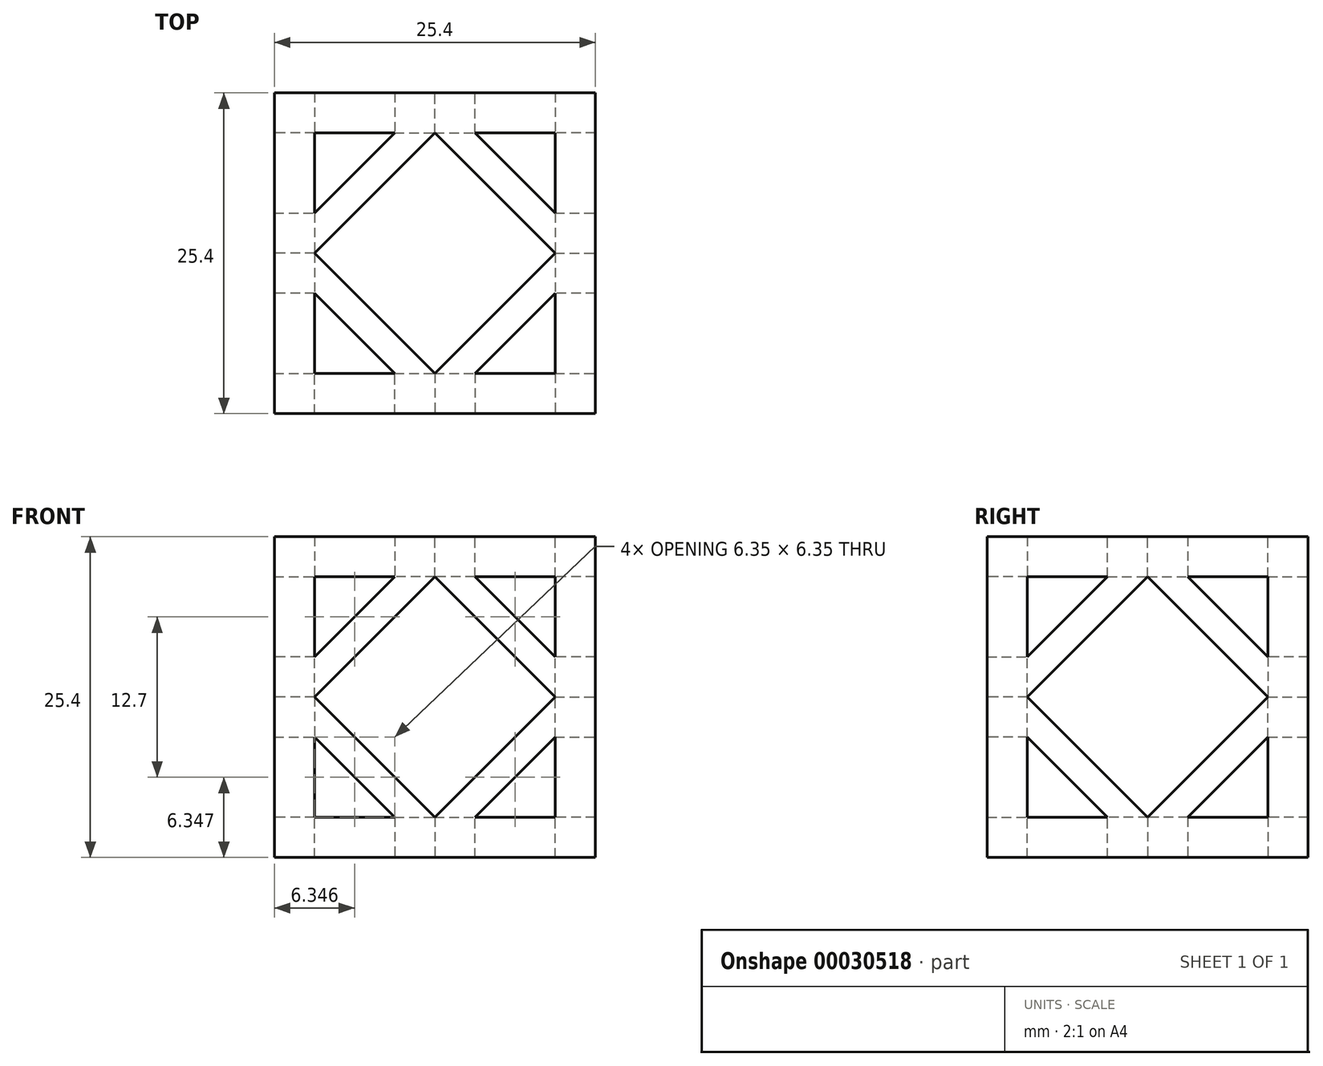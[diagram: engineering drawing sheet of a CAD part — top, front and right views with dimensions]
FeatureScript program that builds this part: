
annotation { "Feature Type Name" : "Feature", "Feature Type Description" : "" }
export const myFeature = defineFeature(function(context is Context, id is Id, definition is map)
    precondition{}
    {
        {
            var Q0;
            Q0=qCreatedBy(makeId("Front.planeOp"),FACE);
            var sketch = newSketch(context, id + "F0", { "sketchPlane" : qUnion([Q0])});
            skLineSegment(sketch, "E0.bottom", {"start": v(-17.45, 16.02) * mm, "end": v(7.95, 16.02) * mm});
            skLineSegment(sketch, "E0.top", {"start": v(-17.45, -9.38) * mm, "end": v(7.95, -9.38) * mm});
            skLineSegment(sketch, "E0.left", {"start": v(-17.45, 16.02) * mm, "end": v(-17.45, -9.38) * mm});
            skLineSegment(sketch, "E0.right", {"start": v(7.95, 16.02) * mm, "end": v(7.95, -9.38) * mm});
            skSolve(sketch);
        }
        {
            var Q0;
            Q0 = qSketchRegion(id + "F0", true);
            extrude(context, id + "F1", {"entities" : qUnion([Q0]), "depth" : 25.4 * mm});
        }
        {
            var Q0;
            Q0=makeQuery(id+"F1.opExtrude","CAP_FACE",FACE,{"disambiguationData":[OSD([sQuery(id+"F0.wireOp",EDGE,"E0.bottom"),sQuery(id+"F0.wireOp",EDGE,"E0.top"),sQuery(id+"F0.wireOp",EDGE,"E0.left"),sQuery(id+"F0.wireOp",EDGE,"E0.right")])],"isStart":false});
            var sketch = newSketch(context, id + "F2", { "sketchPlane" : qUnion([Q0])});
            skLineSegment(sketch, "E1.bottom", {"start": v(-14.28, 12.84) * mm, "end": v(4.77, 12.84) * mm});
            skLineSegment(sketch, "E1.top", {"start": v(-14.28, -6.2) * mm, "end": v(4.77, -6.2) * mm});
            skLineSegment(sketch, "E1.left", {"start": v(-14.28, 12.84) * mm, "end": v(-14.28, -6.2) * mm});
            skLineSegment(sketch, "E1.right", {"start": v(4.77, 12.84) * mm, "end": v(4.77, -6.2) * mm});
            skSolve(sketch);
        }
        {
            var Q0;
            Q0 = qSketchRegion(id + "F2", true);
            extrude(context, id + "F3", {"entities" : qUnion([Q0]), "operationType" : NewBodyOperationType.REMOVE, "oppositeDirection" : true, "depth" : 25.4 * mm});
        }
        {
            var Q0;
            Q0=makeQuery(id+"F1.opExtrude","SWEPT_FACE",FACE,{"disambiguationData":[OSD([sQuery(id+"F0.wireOp",EDGE,"E0.right")])]});
            var sketch = newSketch(context, id + "F4", { "sketchPlane" : qUnion([Q0])});
            skLineSegment(sketch, "E2.bottom", {"start": v(-22.23, 12.84) * mm, "end": v(-3.18, 12.84) * mm});
            skLineSegment(sketch, "E2.top", {"start": v(-22.23, -6.2) * mm, "end": v(-3.18, -6.2) * mm});
            skLineSegment(sketch, "E2.left", {"start": v(-22.23, 12.84) * mm, "end": v(-22.23, -6.2) * mm});
            skLineSegment(sketch, "E2.right", {"start": v(-3.18, 12.84) * mm, "end": v(-3.18, -6.2) * mm});
            skSolve(sketch);
        }
        {
            var Q0;
            Q0 = qSketchRegion(id + "F4", true);
            extrude(context, id + "F5", {"entities" : qUnion([Q0]), "operationType" : NewBodyOperationType.REMOVE, "oppositeDirection" : true, "depth" : 25.4 * mm});
        }
        {
            var Q0;
            Q0=makeQuery(id+"F1.opExtrude","SWEPT_FACE",FACE,{"disambiguationData":[OSD([sQuery(id+"F0.wireOp",EDGE,"E0.bottom")])]});
            var sketch = newSketch(context, id + "F6", { "sketchPlane" : qUnion([Q0])});
            skLineSegment(sketch, "E3.bottom", {"start": v(-14.28, -3.17) * mm, "end": v(4.77, -3.17) * mm});
            skLineSegment(sketch, "E3.top", {"start": v(-14.28, -22.23) * mm, "end": v(4.77, -22.23) * mm});
            skLineSegment(sketch, "E3.left", {"start": v(-14.28, -3.17) * mm, "end": v(-14.28, -22.23) * mm});
            skLineSegment(sketch, "E3.right", {"start": v(4.77, -3.18) * mm, "end": v(4.77, -22.23) * mm});
            skSolve(sketch);
        }
        {
            var Q0;
            Q0 = qSketchRegion(id + "F6", true);
            extrude(context, id + "F7", {"entities" : qUnion([Q0]), "operationType" : NewBodyOperationType.REMOVE, "oppositeDirection" : true, "depth" : 25.4 * mm});
        }
        {
            var Q0;
            Q0=qCreatedBy(makeId("Front.planeOp"),FACE);
            var sketch = newSketch(context, id + "F8", { "sketchPlane" : qUnion([Q0])});
            skLineSegment(sketch, "E4", {"start": v(-4.75, 16.02) * mm, "end": v(-17.45, 3.32) * mm});
            skLineSegment(sketch, "E5", {"start": v(-17.45, 3.32) * mm, "end": v(-4.75, -9.38) * mm});
            skLineSegment(sketch, "E6", {"start": v(-4.75, -9.38) * mm, "end": v(7.95, 3.32) * mm});
            skLineSegment(sketch, "E7", {"start": v(7.95, 3.32) * mm, "end": v(-4.75, 16.02) * mm});
            skLineSegment(sketch, "E8", {"start": v(-4.75, 12.84) * mm, "end": v(-14.28, 3.32) * mm});
            skLineSegment(sketch, "E9", {"start": v(-14.28, 3.32) * mm, "end": v(-4.75, -6.2) * mm});
            skLineSegment(sketch, "E10", {"start": v(-4.75, -6.2) * mm, "end": v(4.77, 3.32) * mm});
            skLineSegment(sketch, "E11", {"start": v(4.77, 3.32) * mm, "end": v(-4.75, 12.84) * mm});
            skSolve(sketch);
        }
        {
            var Q0;
            Q0 = qSketchRegion(id + "F8", true);
            extrude(context, id + "F9", {"entities" : qUnion([Q0]), "operationType" : NewBodyOperationType.ADD, "depth" : 3.17 * mm});
        }
        {
            var Q0;
            Q0=makeQuery(id+"F1.opExtrude","SWEPT_FACE",FACE,{"disambiguationData":[OSD([sQuery(id+"F0.wireOp",EDGE,"E0.right")])]});
            var sketch = newSketch(context, id + "F10", { "sketchPlane" : qUnion([Q0])});
            skLineSegment(sketch, "E12", {"start": v(-12.7, 16.02) * mm, "end": v(-25.4, 3.32) * mm});
            skLineSegment(sketch, "E13", {"start": v(-25.4, 3.32) * mm, "end": v(-12.7, -9.38) * mm});
            skLineSegment(sketch, "E14", {"start": v(-12.7, -9.38) * mm, "end": v(0, 3.32) * mm});
            skLineSegment(sketch, "E15", {"start": v(0, 3.32) * mm, "end": v(-12.7, 16.02) * mm});
            skLineSegment(sketch, "E16", {"start": v(-12.7, 12.84) * mm, "end": v(-22.23, 3.32) * mm});
            skLineSegment(sketch, "E17", {"start": v(-22.23, 3.32) * mm, "end": v(-12.7, -6.2) * mm});
            skLineSegment(sketch, "E18", {"start": v(-12.7, -6.2) * mm, "end": v(-3.18, 3.32) * mm});
            skLineSegment(sketch, "E19", {"start": v(-3.18, 3.32) * mm, "end": v(-12.7, 12.84) * mm});
            skSolve(sketch);
        }
        {
            var Q0;
            Q0 = qSketchRegion(id + "F10", true);
            extrude(context, id + "F11", {"entities" : qUnion([Q0]), "operationType" : NewBodyOperationType.ADD, "oppositeDirection" : true, "depth" : 3.17 * mm});
        }
        {
            var Q0;
            Q0=makeQuery(id+"F1.opExtrude","SWEPT_FACE",FACE,{"disambiguationData":[OSD([sQuery(id+"F0.wireOp",EDGE,"E0.bottom")])]});
            var sketch = newSketch(context, id + "F12", { "sketchPlane" : qUnion([Q0])});
            skLineSegment(sketch, "E20", {"start": v(-4.75, 0) * mm, "end": v(-17.45, -12.7) * mm});
            skLineSegment(sketch, "E21", {"start": v(-17.45, -12.7) * mm, "end": v(-4.75, -25.4) * mm});
            skLineSegment(sketch, "E22", {"start": v(-4.75, -25.4) * mm, "end": v(7.95, -12.7) * mm});
            skLineSegment(sketch, "E23", {"start": v(7.95, -12.7) * mm, "end": v(-4.75, 0) * mm});
            skLineSegment(sketch, "E24", {"start": v(-4.75, -3.18) * mm, "end": v(-14.28, -12.7) * mm});
            skLineSegment(sketch, "E25", {"start": v(-14.28, -12.7) * mm, "end": v(-4.75, -22.23) * mm});
            skLineSegment(sketch, "E26", {"start": v(-4.75, -22.23) * mm, "end": v(4.77, -12.7) * mm});
            skLineSegment(sketch, "E27", {"start": v(4.77, -12.7) * mm, "end": v(-4.75, -3.18) * mm});
            skSolve(sketch);
        }
        {
            var Q0;
            Q0 = qSketchRegion(id + "F12", true);
            extrude(context, id + "F13", {"entities" : qUnion([Q0]), "operationType" : NewBodyOperationType.ADD, "oppositeDirection" : true, "depth" : 3.17 * mm});
        }
        {
            var Q0;
            Q0=makeQuery(id+"F1.opExtrude","SWEPT_FACE",FACE,{"disambiguationData":[OSD([sQuery(id+"F0.wireOp",EDGE,"E0.left")])]});
            var sketch = newSketch(context, id + "F14", { "sketchPlane" : qUnion([Q0])});
            skLineSegment(sketch, "E28", {"start": v(12.7, 16.02) * mm, "end": v(0, 3.32) * mm});
            skLineSegment(sketch, "E29", {"start": v(0, 3.32) * mm, "end": v(12.7, -9.38) * mm});
            skLineSegment(sketch, "E30", {"start": v(12.7, -9.38) * mm, "end": v(25.4, 3.32) * mm});
            skLineSegment(sketch, "E31", {"start": v(25.4, 3.32) * mm, "end": v(12.7, 16.02) * mm});
            skLineSegment(sketch, "E32", {"start": v(12.7, 12.84) * mm, "end": v(3.18, 3.32) * mm});
            skLineSegment(sketch, "E33", {"start": v(3.18, 3.32) * mm, "end": v(12.7, -6.2) * mm});
            skLineSegment(sketch, "E34", {"start": v(12.7, -6.2) * mm, "end": v(22.23, 3.32) * mm});
            skLineSegment(sketch, "E35", {"start": v(22.23, 3.32) * mm, "end": v(12.7, 12.84) * mm});
            skSolve(sketch);
        }
        {
            var Q0;
            Q0 = qSketchRegion(id + "F14", true);
            extrude(context, id + "F15", {"entities" : qUnion([Q0]), "operationType" : NewBodyOperationType.ADD, "oppositeDirection" : true, "depth" : 3.17 * mm});
        }
        {
            var Q0;
            Q0=makeQuery(id+"F1.opExtrude","CAP_FACE",FACE,{"disambiguationData":[OSD([sQuery(id+"F0.wireOp",EDGE,"E0.bottom"),sQuery(id+"F0.wireOp",EDGE,"E0.top"),sQuery(id+"F0.wireOp",EDGE,"E0.left"),sQuery(id+"F0.wireOp",EDGE,"E0.right")])],"isStart":false});
            var sketch = newSketch(context, id + "F16", { "sketchPlane" : qUnion([Q0])});
            skLineSegment(sketch, "E36", {"start": v(-4.75, 16.02) * mm, "end": v(-17.45, 3.32) * mm});
            skLineSegment(sketch, "E37", {"start": v(-17.45, 3.32) * mm, "end": v(-4.75, -9.38) * mm});
            skLineSegment(sketch, "E38", {"start": v(-4.75, -9.38) * mm, "end": v(7.95, 3.32) * mm});
            skLineSegment(sketch, "E39", {"start": v(7.95, 3.32) * mm, "end": v(-4.75, 16.02) * mm});
            skLineSegment(sketch, "E40", {"start": v(-4.75, 12.84) * mm, "end": v(-14.28, 3.32) * mm});
            skLineSegment(sketch, "E41", {"start": v(-14.28, 3.32) * mm, "end": v(-4.75, -6.2) * mm});
            skLineSegment(sketch, "E42", {"start": v(-4.75, -6.2) * mm, "end": v(4.77, 3.32) * mm});
            skLineSegment(sketch, "E43", {"start": v(4.77, 3.32) * mm, "end": v(-4.75, 12.84) * mm});
            skSolve(sketch);
        }
        {
            var Q0;
            Q0 = qSketchRegion(id + "F16", true);
            extrude(context, id + "F17", {"entities" : qUnion([Q0]), "operationType" : NewBodyOperationType.ADD, "oppositeDirection" : true, "depth" : 3.17 * mm});
        }
        {
            var Q0;
            Q0=makeQuery(id+"F1.opExtrude","SWEPT_FACE",FACE,{"disambiguationData":[OSD([sQuery(id+"F0.wireOp",EDGE,"E0.top")])]});
            var sketch = newSketch(context, id + "F18", { "sketchPlane" : qUnion([Q0])});
            skLineSegment(sketch, "E44", {"start": v(-4.75, 25.4) * mm, "end": v(-17.45, 12.7) * mm});
            skLineSegment(sketch, "E45", {"start": v(-17.45, 12.7) * mm, "end": v(-4.75, 0) * mm});
            skLineSegment(sketch, "E46", {"start": v(-4.75, 0) * mm, "end": v(7.95, 12.7) * mm});
            skLineSegment(sketch, "E47", {"start": v(7.95, 12.7) * mm, "end": v(-4.75, 25.4) * mm});
            skLineSegment(sketch, "E48", {"start": v(-4.75, 22.23) * mm, "end": v(-14.28, 12.7) * mm});
            skLineSegment(sketch, "E49", {"start": v(-14.28, 12.7) * mm, "end": v(-4.75, 3.18) * mm});
            skLineSegment(sketch, "E50", {"start": v(-4.75, 3.18) * mm, "end": v(4.77, 12.7) * mm});
            skLineSegment(sketch, "E51", {"start": v(4.77, 12.7) * mm, "end": v(-4.75, 22.23) * mm});
            skSolve(sketch);
        }
        {
            var Q0;
            Q0 = qSketchRegion(id + "F18", true);
            extrude(context, id + "F19", {"entities" : qUnion([Q0]), "operationType" : NewBodyOperationType.ADD, "oppositeDirection" : true, "depth" : 3.17 * mm});
        }
    });
